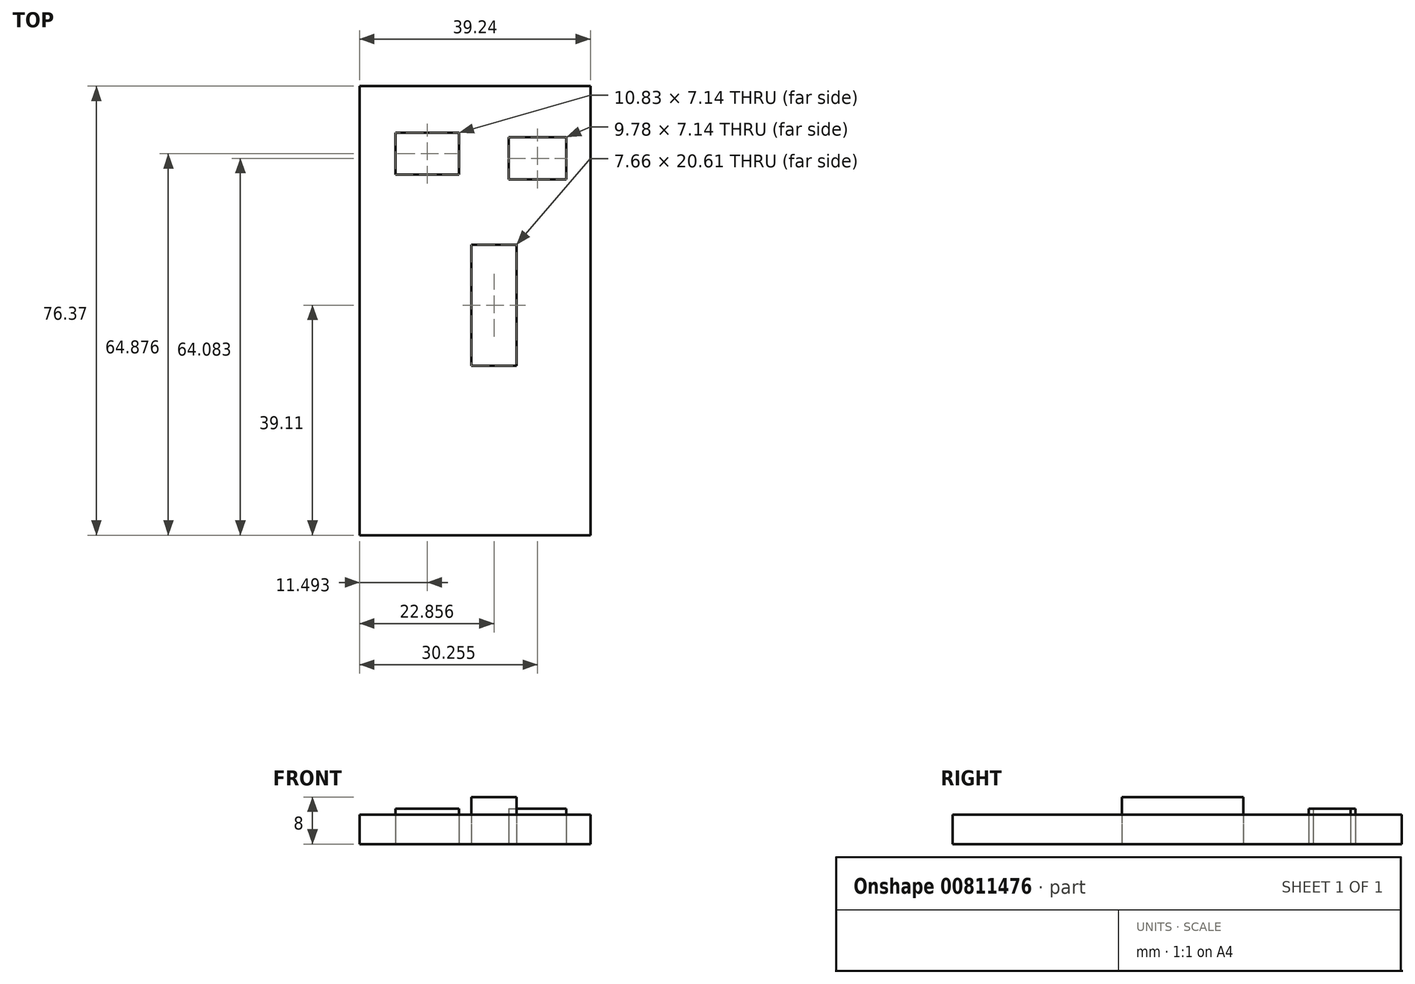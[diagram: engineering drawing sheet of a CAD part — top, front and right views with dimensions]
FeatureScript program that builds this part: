
annotation { "Feature Type Name" : "Feature", "Feature Type Description" : "" }
export const myFeature = defineFeature(function(context is Context, id is Id, definition is map)
    precondition{}
    {
        {
            var Q0;
            Q0=qCreatedBy(makeId("Top.planeOp"),FACE);
            var sketch = newSketch(context, id + "F0", { "sketchPlane" : qUnion([Q0])});
            skLineSegment(sketch, "E0.bottom", {"start": v(-39.24, -16.78) * mm, "end": v(0, -16.78) * mm});
            skLineSegment(sketch, "E0.top", {"start": v(-39.24, 59.6) * mm, "end": v(0, 59.6) * mm});
            skLineSegment(sketch, "E0.left", {"start": v(-39.24, -16.78) * mm, "end": v(-39.24, 59.6) * mm});
            skLineSegment(sketch, "E0.right", {"start": v(0, -16.78) * mm, "end": v(0, 59.6) * mm});
            skLineSegment(sketch, "E1.bottom", {"start": v(-33.16, 51.66) * mm, "end": v(-22.33, 51.66) * mm});
            skLineSegment(sketch, "E1.top", {"start": v(-33.16, 44.53) * mm, "end": v(-22.33, 44.53) * mm});
            skLineSegment(sketch, "E1.left", {"start": v(-33.16, 51.66) * mm, "end": v(-33.16, 44.53) * mm});
            skLineSegment(sketch, "E1.right", {"start": v(-22.33, 51.66) * mm, "end": v(-22.33, 44.53) * mm});
            skLineSegment(sketch, "E2.bottom", {"start": v(-13.87, 50.87) * mm, "end": v(-4.1, 50.87) * mm});
            skLineSegment(sketch, "E2.top", {"start": v(-13.87, 43.74) * mm, "end": v(-4.1, 43.74) * mm});
            skLineSegment(sketch, "E2.left", {"start": v(-13.87, 50.87) * mm, "end": v(-13.87, 43.74) * mm});
            skLineSegment(sketch, "E2.right", {"start": v(-4.1, 50.87) * mm, "end": v(-4.1, 43.74) * mm});
            skLineSegment(sketch, "E3.bottom", {"start": v(-20.22, 32.64) * mm, "end": v(-12.55, 32.64) * mm});
            skLineSegment(sketch, "E3.top", {"start": v(-20.22, 12.02) * mm, "end": v(-12.55, 12.02) * mm});
            skLineSegment(sketch, "E3.left", {"start": v(-20.22, 32.64) * mm, "end": v(-20.22, 12.02) * mm});
            skLineSegment(sketch, "E3.right", {"start": v(-12.55, 32.64) * mm, "end": v(-12.55, 12.02) * mm});
            skSolve(sketch);
        }
        {
            var Q0;
            Q0=makeQuery(id+"F0.imprint","IMPRINT",FACE,{"disambiguationData":[TD([[makeQuery(id+"F0.imprint","IMPRINT",EDGE,{"derivedFrom":sQuery(id+"F0.wireOp",EDGE,"E3.bottom")}),-1.0]])]});
            extrude(context, id + "F1", {"entities" : qUnion([Q0]), "depth" : 8 * mm, "offsetDistance" : 25 * mm});
        }
        {
            var Q0;
            Q0=makeQuery(id+"F0.imprint","IMPRINT",FACE,{"disambiguationData":[TD([[makeQuery(id+"F0.imprint","IMPRINT",EDGE,{"derivedFrom":sQuery(id+"F0.wireOp",EDGE,"E1.bottom")}),-1.0]])]});
            var Q1;
            Q1=makeQuery(id+"F0.imprint","IMPRINT",FACE,{"disambiguationData":[TD([[makeQuery(id+"F0.imprint","IMPRINT",EDGE,{"derivedFrom":sQuery(id+"F0.wireOp",EDGE,"E2.bottom")}),-1.0]])]});
            extrude(context, id + "F2", {"entities" : qUnion([Q0, Q1]), "depth" : 6 * mm, "offsetDistance" : 25 * mm});
        }
        {
            var Q0;
            Q0=makeQuery(id+"F0.imprint","IMPRINT",FACE,{"disambiguationData":[TD([[makeQuery(id+"F0.imprint","IMPRINT",EDGE,{"derivedFrom":sQuery(id+"F0.wireOp",EDGE,"E0.bottom")}),1.0]])]});
            extrude(context, id + "F3", {"entities" : qUnion([Q0]), "depth" : 5 * mm, "offsetDistance" : 25 * mm});
        }
    });
